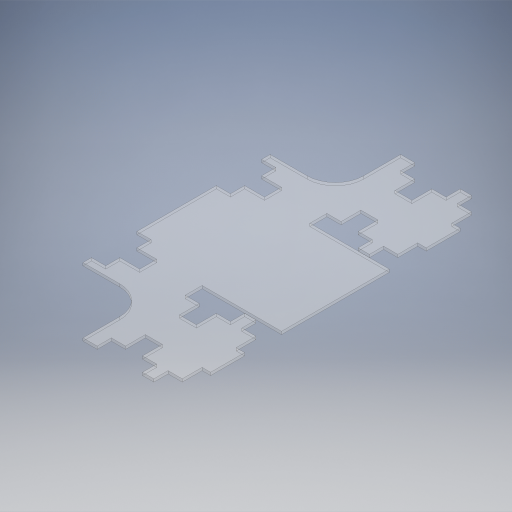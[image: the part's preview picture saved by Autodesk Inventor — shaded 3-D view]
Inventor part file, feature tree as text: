
AUTODESK INVENTOR PART (.ipt)
format: ipt  version: 2024.2 (Build 282272000, 272)  size: 824,832 bytes
history: native  units: in
note: dims shown in document units (in); Inventor stores cm internally (conversion verified against a paired STEP export)
features: extrude x9, sketch x9, projected_geometry x8
ambient origin geometry x8: Origin, YZ Plane, XZ Plane, XY Plane, X Axis, Y Axis, Z Axis, Center Point
bodies: Solid1 (feature_tree)
feature tree (26):
  extrude  "Extrusion1"  Depth=28.0in
  extrude  "Extrusion2"  Depth=3.0in
  extrude  "Extrusion3"  Depth=1.75in
  extrude  "Extrusion4"  Depth=0.25in TaperAngle=0.0deg
  extrude  "Extrusion5"  Depth=1.25in
  extrude  "Extrusion6"  Depth=1.75in
  extrude  "Extrusion7"  Depth=1.25in
  extrude  "Extrusion8"  Depth=5.75in
  extrude  "Extrusion9"  Depth=2.5in
  sketch  "Sketch1"  dims[d0=28.0in d1=28.0in]
  sketch  "Sketch2"  dims[d2=0.25in d3=0.0in d4=3.0in]
  projected_geometry  "Projected Loop1"
  sketch  "Sketch3"  dims[d5=1.25in d6=1.75in]
  projected_geometry  "Projected Loop2"
  sketch  "Sketch4"  dims[d7=1.75in d8=0.25in d9=0.0in]
  projected_geometry  "Projected Loop3"
  sketch  "Sketch5"  dims[d10=6.5in d11=1.25in]
  projected_geometry  "Projected Loop4"
  sketch  "Sketch6"  dims[d12=1.25in d13=1.75in]
  projected_geometry  "Projected Loop5"
  sketch  "Sketch7"  dims[d14=1.5in d15=1.25in]
  projected_geometry  "Projected Loop6"
  sketch  "Sketch8"  dims[d16=0.25in d17=0.0in d18=5.75in]
  projected_geometry  "Projected Loop7"
  sketch  "Sketch9"  dims[d19=5.75in d20=2.5in d21=0.25in d22=0.0in d24=6.25in d25=1.25in d26=1.25in d27=1.05in d30=1.5in d33=1.707in d34=0.846in d35=22.6875in d36=0.0in d38=6.625in d39=14.375in d40=0.0in d42=0.25in d43=0.25in d44=0.5in d45=1.25in d46=1.147in d47=1.25in d48=1.75in d49=1.5in d50=1.75in d51=1.25in d52=0.5in d53=0.5in d54=14.375in d55=0.0in d56=1.5in d57=1.0in d58=0.0in d59=0.9375in d60=0.0in d61=0.5in d62=0.0344in]
  projected_geometry  "Projected Loop8"
